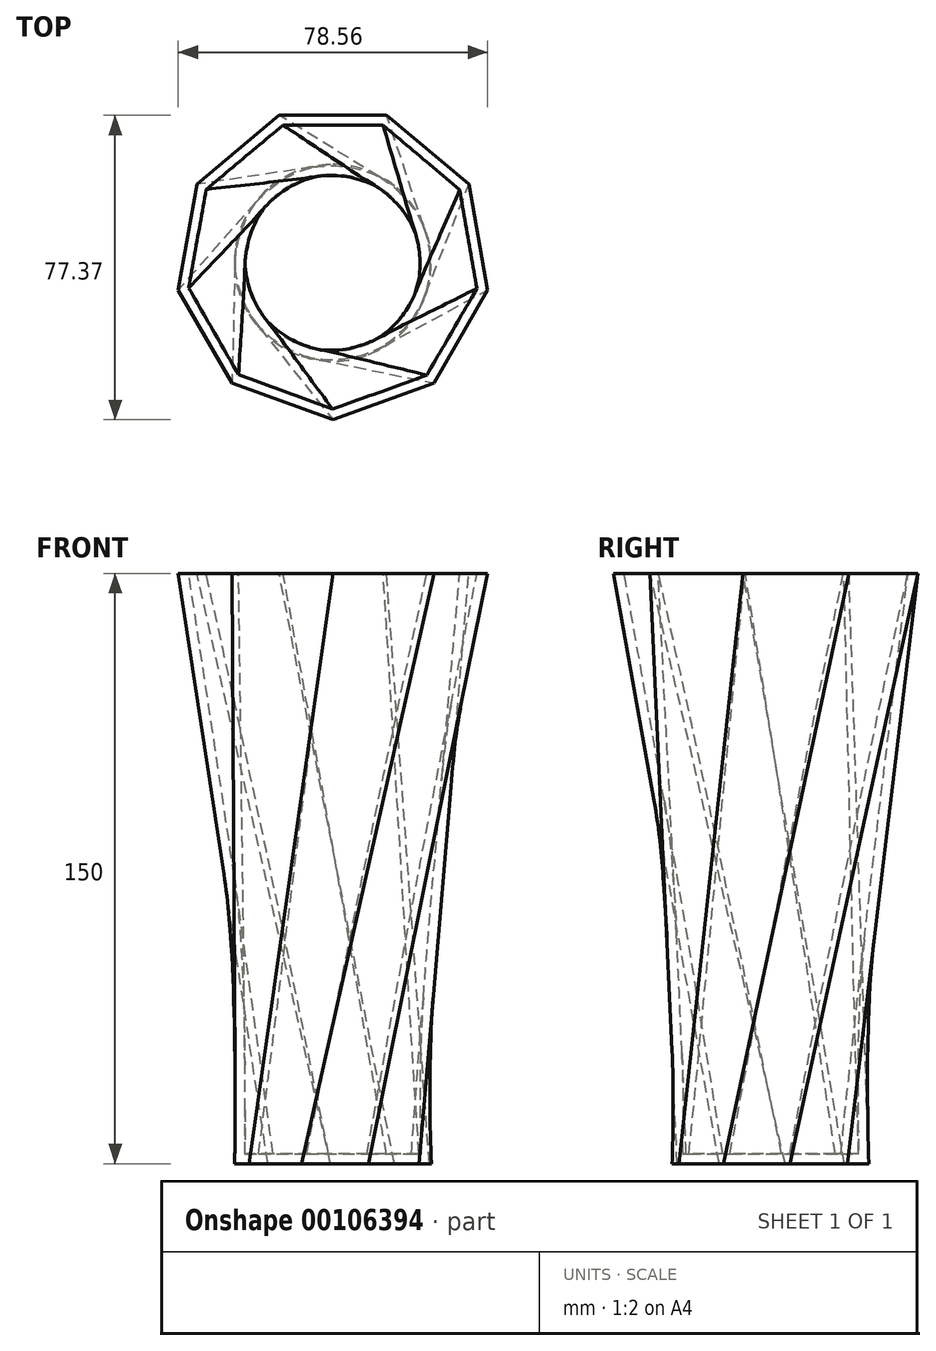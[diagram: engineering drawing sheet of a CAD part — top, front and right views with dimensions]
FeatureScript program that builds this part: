
annotation { "Feature Type Name" : "Feature", "Feature Type Description" : "" }
export const myFeature = defineFeature(function(context is Context, id is Id, definition is map)
    precondition{}
    {
        {
            var Q0;
            Q0=qCreatedBy(makeId("Top.planeOp"),FACE);
            var sketch = newSketch(context, id + "F0", { "sketchPlane" : qUnion([Q0])});
            skCircle(sketch, "E0", {"center": v(0, 0) * mm, "radius": 25 * mm});
            skPoint(sketch, "E1", {"position": v(-8, -23.69) * mm});
            skSolve(sketch);
        }
        {
            var Q0;
            Q0=qCreatedBy(makeId("Top.planeOp"),FACE);
            cPlane(context, id + "F1", {"entities" : qUnion([Q0]), "cplaneType" : CPlaneType.OFFSET, "offset" : 150 * mm, "width" : 150 * mm, "height" : 150 * mm});
        }
        {
            var Q0;
            Q0=qCreatedBy(id+"F1.planeOp",FACE);
            var sketch = newSketch(context, id + "F2", { "sketchPlane" : qUnion([Q0])});
            skCircle(sketch, "E2.cCircle", {"center": v(0, 0) * mm, "radius": 37.48 * mm, "construction": true});
            skLineSegment(sketch, "E2.0", {"start": v(-13.64, 37.48) * mm, "end": v(13.64, 37.48) * mm});
            skLineSegment(sketch, "E2.1", {"start": v(13.64, 37.48) * mm, "end": v(34.54, 19.94) * mm});
            skLineSegment(sketch, "E2.2", {"start": v(34.54, 19.94) * mm, "end": v(39.28, -6.93) * mm});
            skLineSegment(sketch, "E2.3", {"start": v(39.28, -6.93) * mm, "end": v(25.64, -30.56) * mm});
            skLineSegment(sketch, "E2.4", {"start": v(25.64, -30.56) * mm, "end": v(0, -39.89) * mm});
            skLineSegment(sketch, "E2.5", {"start": v(0, -39.89) * mm, "end": v(-25.64, -30.56) * mm});
            skLineSegment(sketch, "E2.6", {"start": v(-25.64, -30.56) * mm, "end": v(-39.28, -6.93) * mm});
            skLineSegment(sketch, "E2.7", {"start": v(-39.28, -6.93) * mm, "end": v(-34.54, 19.94) * mm});
            skLineSegment(sketch, "E2.8", {"start": v(-34.54, 19.94) * mm, "end": v(-13.64, 37.48) * mm});
            skPoint(sketch, "E2.0.midPoint", {"position": v(0, 37.48) * mm});
            skSolve(sketch);
        }
        {
            var Q0;
            Q0=makeQuery(id+"F0.imprint","IMPRINT",FACE,{"disambiguationData":[TD([[makeQuery(id+"F0.imprint","IMPRINT",EDGE,{"derivedFrom":sQuery(id+"F0.wireOp",EDGE,"E0")}),1.0]])]});
            var Q1;
            Q1=makeQuery(id+"F2.imprint","IMPRINT",FACE,{"disambiguationData":[TD([[makeQuery(id+"F2.imprint","IMPRINT",EDGE,{"derivedFrom":sQuery(id+"F2.wireOp",EDGE,"E2.0")}),-1.0]])]});
            var Q2;
            Q2=sQuery(id+"F0.wireOp",VERTEX,"E1");
            var Q3;
            Q3=sQuery(id+"F2.wireOp",VERTEX,"E2.4.start");
            loft(context, id + "F3", {"sheetProfilesArray" : [{ "sheetProfileEntities" : qUnion([Q0]) }, { "sheetProfileEntities" : qUnion([Q1]) }], "matchConnections" : true, "connections" : [{ "connectionEntities" : qUnion([Q2, Q3]), "connectionEdgeQueries" : qUnion([]), "connectionEdgeParameters" : [] }]});
        }
        {
            var Q0;
            Q0=makeQuery(id+"F3.opLoft","CAP_FACE",FACE,{"disambiguationData":[OSD([makeQuery(id+"F2.imprint","IMPRINT",FACE,{"disambiguationData":[TD([[makeQuery(id+"F2.imprint","IMPRINT",EDGE,{"derivedFrom":sQuery(id+"F2.wireOp",EDGE,"E2.0")}),-1.0]])]})])],"isStart":true});
            shell(context, id + "F4", {"entities" : qUnion([Q0]), "thickness" : 2.5 * mm});
        }
    });
